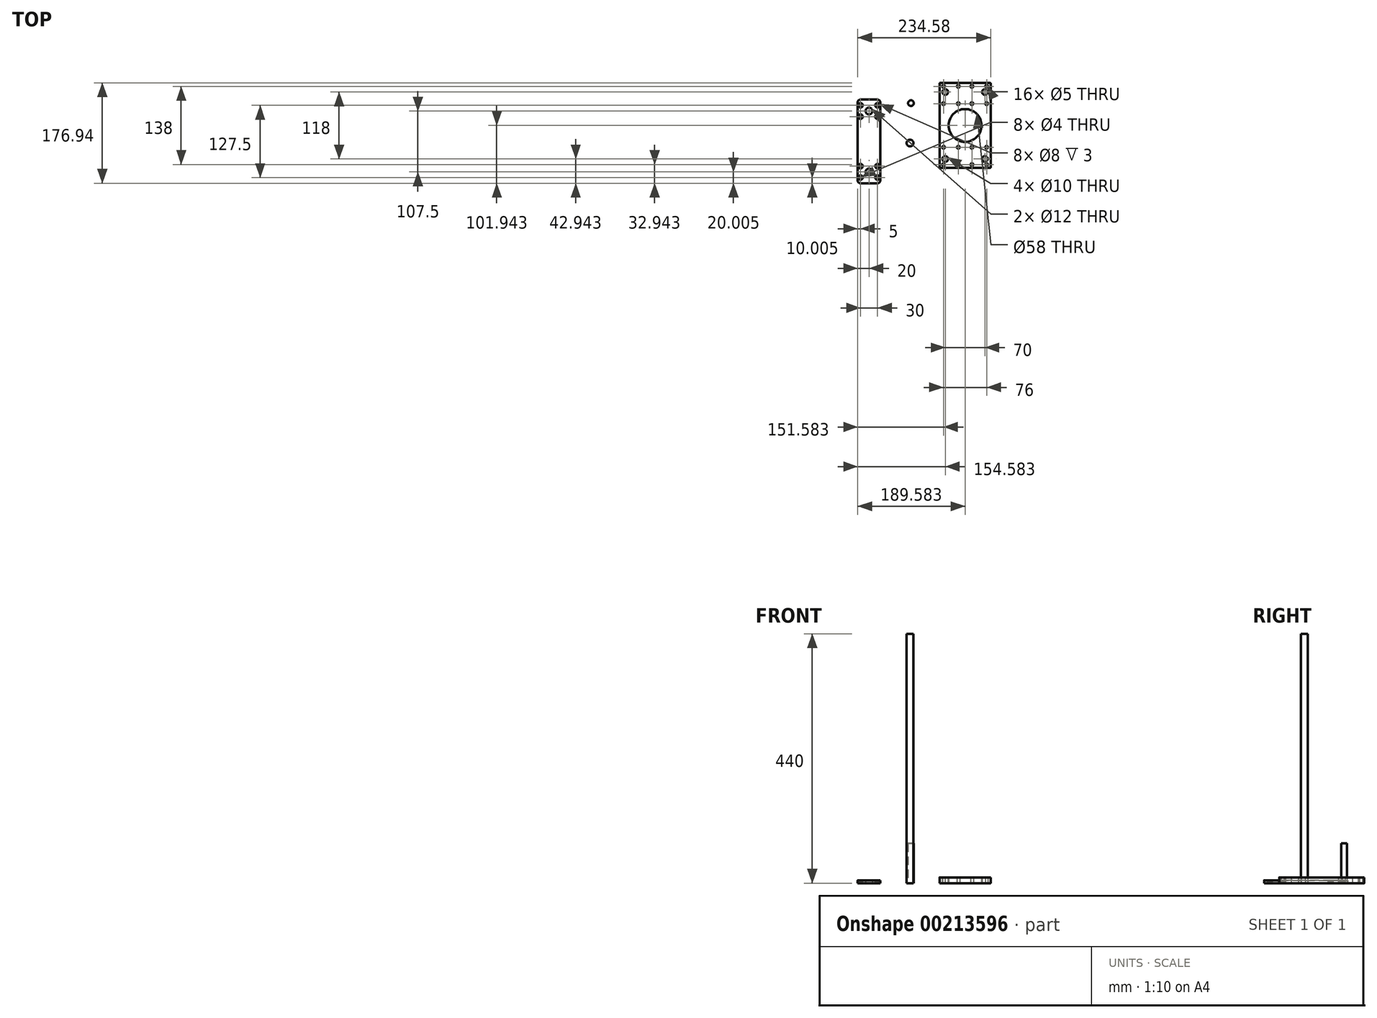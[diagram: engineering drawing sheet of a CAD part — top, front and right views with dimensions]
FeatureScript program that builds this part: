
annotation { "Feature Type Name" : "Feature", "Feature Type Description" : "" }
export const myFeature = defineFeature(function(context is Context, id is Id, definition is map)
    precondition{}
    {
        {
            var Q0;
            Q0=qCreatedBy(makeId("Top.planeOp"),FACE);
            var sketch = newSketch(context, id + "F0", { "sketchPlane" : qUnion([Q0])});
            skLineSegment(sketch, "E0", {"start": v(-47.78, -43.52) * mm, "end": v(42.22, -43.52) * mm});
            skLineSegment(sketch, "E1", {"start": v(42.22, -43.52) * mm, "end": v(42.22, 106.48) * mm});
            skLineSegment(sketch, "E2", {"start": v(42.22, 106.48) * mm, "end": v(-47.78, 106.48) * mm});
            skLineSegment(sketch, "E3", {"start": v(-47.78, 106.48) * mm, "end": v(-47.78, -43.52) * mm});
            skLineSegment(sketch, "E4", {"start": v(-2.78, 106.48) * mm, "end": v(-2.78, -43.52) * mm, "construction": true});
            skCircle(sketch, "E5", {"center": v(-2.78, 31.48) * mm, "radius": 29 * mm});
            skCircle(sketch, "E6", {"center": v(35.22, 100.48) * mm, "radius": 2.5 * mm});
            skCircle(sketch, "E7", {"center": v(35.22, 69.98) * mm, "radius": 2.5 * mm});
            skCircle(sketch, "E8", {"center": v(9.22, 100.48) * mm, "radius": 2.5 * mm});
            skCircle(sketch, "E9", {"center": v(9.22, 69.98) * mm, "radius": 2.5 * mm});
            skCircle(sketch, "E10", {"center": v(-14.78, 100.48) * mm, "radius": 2.5 * mm});
            skCircle(sketch, "E11", {"center": v(-14.78, 69.98) * mm, "radius": 2.5 * mm});
            skCircle(sketch, "E12", {"center": v(-40.78, 100.48) * mm, "radius": 2.5 * mm});
            skCircle(sketch, "E13", {"center": v(-40.78, 69.98) * mm, "radius": 2.5 * mm});
            skCircle(sketch, "E14", {"center": v(35.22, -7.02) * mm, "radius": 2.5 * mm});
            skCircle(sketch, "E15", {"center": v(35.22, -37.52) * mm, "radius": 2.5 * mm});
            skCircle(sketch, "E16", {"center": v(9.22, -7.02) * mm, "radius": 2.5 * mm});
            skCircle(sketch, "E17", {"center": v(9.22, -37.52) * mm, "radius": 2.5 * mm});
            skCircle(sketch, "E18", {"center": v(-14.78, -37.52) * mm, "radius": 2.5 * mm});
            skCircle(sketch, "E19", {"center": v(-40.78, -7.02) * mm, "radius": 2.5 * mm});
            skCircle(sketch, "E20", {"center": v(-40.78, -37.52) * mm, "radius": 2.5 * mm});
            skCircle(sketch, "E21", {"center": v(-14.78, -7.02) * mm, "radius": 2.5 * mm});
            skCircle(sketch, "E22", {"center": v(-37.78, -27.52) * mm, "radius": 5 * mm});
            skCircle(sketch, "E23", {"center": v(32.22, -27.52) * mm, "radius": 5 * mm});
            skCircle(sketch, "E24", {"center": v(32.22, 90.48) * mm, "radius": 5 * mm});
            skCircle(sketch, "E25", {"center": v(-37.78, 90.48) * mm, "radius": 5 * mm});
            skSolve(sketch);
        }
        {
            var Q0;
            Q0=makeQuery(id+"F0.imprint","IMPRINT",FACE,{"disambiguationData":[TD([[makeQuery(id+"F0.imprint","IMPRINT",EDGE,{"derivedFrom":sQuery(id+"F0.wireOp",EDGE,"E0")}),1.0]])]});
            extrude(context, id + "F1", {"entities" : qUnion([Q0]), "depth" : 10 * mm});
        }
        {
            var Q0;
            Q0=makeQuery(id+"F1.opExtrude","SWEPT_EDGE",EDGE,{"disambiguationData":[OSD([sQuery(id+"F0.wireOp",EDGE,"E0"),sQuery(id+"F0.wireOp",EDGE,"E1")])]});
            var Q1;
            Q1=makeQuery(id+"F1.opExtrude","SWEPT_EDGE",EDGE,{"disambiguationData":[OSD([sQuery(id+"F0.wireOp",EDGE,"E1"),sQuery(id+"F0.wireOp",EDGE,"E2")])]});
            var Q2;
            Q2=makeQuery(id+"F1.opExtrude","SWEPT_EDGE",EDGE,{"disambiguationData":[OSD([sQuery(id+"F0.wireOp",EDGE,"E2"),sQuery(id+"F0.wireOp",EDGE,"E3")])]});
            var Q3;
            Q3=makeQuery(id+"F1.opExtrude","SWEPT_EDGE",EDGE,{"disambiguationData":[OSD([sQuery(id+"F0.wireOp",EDGE,"E0"),sQuery(id+"F0.wireOp",EDGE,"E3")])]});
            fillet(context, id + "F2", {"entities" : qUnion([Q0, Q1, Q2, Q3]), "radius" : 1 * mm, "tangentPropagation" : true, "allowEdgeOverflow" : false});
        }
        {
            var Q0;
            Q0=qCreatedBy(makeId("Top.planeOp"),FACE);
            var sketch = newSketch(context, id + "F3", { "sketchPlane" : qUnion([Q0])});
            skCircle(sketch, "E26", {"center": v(-98.34, 70.82) * mm, "radius": 5 * mm});
            skSolve(sketch);
        }
        {
            var Q0;
            Q0=makeQuery(id+"F3.imprint","IMPRINT",FACE,{"disambiguationData":[TD([[makeQuery(id+"F3.imprint","IMPRINT",EDGE,{"derivedFrom":sQuery(id+"F3.wireOp",EDGE,"E26")}),1.0]])]});
            extrude(context, id + "F4", {"entities" : qUnion([Q0]), "depth" : 70 * mm});
        }
        {
            var Q0;
            Q0=qCreatedBy(makeId("Top.planeOp"),FACE);
            var sketch = newSketch(context, id + "F5", { "sketchPlane" : qUnion([Q0])});
            skLineSegment(sketch, "E27", {"start": v(-152.36, 77.04) * mm, "end": v(-152.36, -70.46) * mm});
            skLineSegment(sketch, "E28", {"start": v(-152.36, -70.46) * mm, "end": v(-192.36, -70.46) * mm});
            skLineSegment(sketch, "E29", {"start": v(-192.36, -70.46) * mm, "end": v(-192.36, 77.04) * mm});
            skLineSegment(sketch, "E30", {"start": v(-192.36, 77.04) * mm, "end": v(-152.36, 77.04) * mm});
            skCircle(sketch, "E31", {"center": v(-172.36, 57.04) * mm, "radius": 6 * mm});
            skCircle(sketch, "E32", {"center": v(-172.36, -50.46) * mm, "radius": 6 * mm});
            skCircle(sketch, "E33", {"center": v(-157.36, 67.04) * mm, "radius": 2 * mm});
            skCircle(sketch, "E34", {"center": v(-157.36, 47.04) * mm, "radius": 2 * mm});
            skCircle(sketch, "E35", {"center": v(-187.36, 67.04) * mm, "radius": 2 * mm});
            skCircle(sketch, "E36", {"center": v(-187.36, 47.04) * mm, "radius": 2 * mm});
            skCircle(sketch, "E37", {"center": v(-157.36, -40.46) * mm, "radius": 2 * mm});
            skCircle(sketch, "E38", {"center": v(-187.36, -40.46) * mm, "radius": 2 * mm});
            skCircle(sketch, "E39", {"center": v(-187.36, -60.46) * mm, "radius": 2 * mm});
            skCircle(sketch, "E40", {"center": v(-157.36, -60.46) * mm, "radius": 2 * mm});
            skSolve(sketch);
        }
        {
            var Q0;
            Q0=makeQuery(id+"F5.imprint","IMPRINT",FACE,{"disambiguationData":[TD([[makeQuery(id+"F5.imprint","IMPRINT",EDGE,{"derivedFrom":sQuery(id+"F5.wireOp",EDGE,"E27")}),-1.0]])]});
            extrude(context, id + "F6", {"entities" : qUnion([Q0]), "depth" : 5 * mm});
        }
        {
            var Q0;
            Q0=makeQuery(id+"F6.opExtrude","SWEPT_EDGE",EDGE,{"disambiguationData":[OSD([sQuery(id+"F5.wireOp",EDGE,"E29"),sQuery(id+"F5.wireOp",EDGE,"E30")])]});
            var Q1;
            Q1=makeQuery(id+"F6.opExtrude","SWEPT_EDGE",EDGE,{"disambiguationData":[OSD([sQuery(id+"F5.wireOp",EDGE,"E28"),sQuery(id+"F5.wireOp",EDGE,"E29")])]});
            var Q2;
            Q2=makeQuery(id+"F6.opExtrude","SWEPT_EDGE",EDGE,{"disambiguationData":[OSD([sQuery(id+"F5.wireOp",EDGE,"E27"),sQuery(id+"F5.wireOp",EDGE,"E28")])]});
            var Q3;
            Q3=makeQuery(id+"F6.opExtrude","SWEPT_EDGE",EDGE,{"disambiguationData":[OSD([sQuery(id+"F5.wireOp",EDGE,"E27"),sQuery(id+"F5.wireOp",EDGE,"E30")])]});
            fillet(context, id + "F7", {"entities" : qUnion([Q0, Q1, Q2, Q3]), "radius" : 5 * mm, "tangentPropagation" : true, "allowEdgeOverflow" : false});
        }
        {
            var Q0;
            Q0=makeQuery(id+"F6.opExtrude","CAP_FACE",FACE,{"disambiguationData":[OSD([sQuery(id+"F5.wireOp",EDGE,"E27"),sQuery(id+"F5.wireOp",EDGE,"E28"),sQuery(id+"F5.wireOp",EDGE,"E29"),sQuery(id+"F5.wireOp",EDGE,"E30"),sQuery(id+"F5.wireOp",EDGE,"E31"),sQuery(id+"F5.wireOp",EDGE,"E32"),sQuery(id+"F5.wireOp",EDGE,"E33"),sQuery(id+"F5.wireOp",EDGE,"E34"),sQuery(id+"F5.wireOp",EDGE,"E35"),sQuery(id+"F5.wireOp",EDGE,"E36"),sQuery(id+"F5.wireOp",EDGE,"E37"),sQuery(id+"F5.wireOp",EDGE,"E38"),sQuery(id+"F5.wireOp",EDGE,"E39"),sQuery(id+"F5.wireOp",EDGE,"E40")])],"isStart":false});
            var sketch = newSketch(context, id + "F8", { "sketchPlane" : qUnion([Q0])});
            skCircle(sketch, "E41", {"center": v(-157.36, 67.04) * mm, "radius": 4 * mm});
            skCircle(sketch, "E42", {"center": v(-157.36, 47.04) * mm, "radius": 4 * mm});
            skCircle(sketch, "E43", {"center": v(-187.36, 47.04) * mm, "radius": 4 * mm});
            skCircle(sketch, "E44", {"center": v(-187.36, 67.04) * mm, "radius": 4 * mm});
            skCircle(sketch, "E45", {"center": v(-187.36, -40.46) * mm, "radius": 4 * mm});
            skCircle(sketch, "E46", {"center": v(-187.36, -60.46) * mm, "radius": 4 * mm});
            skCircle(sketch, "E47", {"center": v(-157.36, -60.46) * mm, "radius": 4 * mm});
            skCircle(sketch, "E48", {"center": v(-157.36, -40.46) * mm, "radius": 4 * mm});
            skSolve(sketch);
        }
        {
            var Q0;
            Q0=makeQuery(id+"F8.imprint","IMPRINT",FACE,{"disambiguationData":[TD([[makeQuery(id+"F8.imprint","IMPRINT",EDGE,{"derivedFrom":sQuery(id+"F8.wireOp",EDGE,"E41")}),1.0]])]});
            var Q1;
            Q1=makeQuery(id+"F8.imprint","IMPRINT",FACE,{"disambiguationData":[TD([[makeQuery(id+"F8.imprint","IMPRINT",EDGE,{"derivedFrom":sQuery(id+"F8.wireOp",EDGE,"E42")}),1.0]])]});
            var Q2;
            Q2=makeQuery(id+"F8.imprint","IMPRINT",FACE,{"disambiguationData":[TD([[makeQuery(id+"F8.imprint","IMPRINT",EDGE,{"derivedFrom":sQuery(id+"F8.wireOp",EDGE,"E43")}),1.0]])]});
            var Q3;
            Q3=makeQuery(id+"F8.imprint","IMPRINT",FACE,{"disambiguationData":[TD([[makeQuery(id+"F8.imprint","IMPRINT",EDGE,{"derivedFrom":sQuery(id+"F8.wireOp",EDGE,"E44")}),1.0]])]});
            var Q4;
            Q4=makeQuery(id+"F8.imprint","IMPRINT",FACE,{"disambiguationData":[TD([[makeQuery(id+"F8.imprint","IMPRINT",EDGE,{"derivedFrom":sQuery(id+"F8.wireOp",EDGE,"E45")}),1.0]])]});
            var Q5;
            Q5=makeQuery(id+"F8.imprint","IMPRINT",FACE,{"disambiguationData":[TD([[makeQuery(id+"F8.imprint","IMPRINT",EDGE,{"derivedFrom":sQuery(id+"F8.wireOp",EDGE,"E48")}),1.0]])]});
            var Q6;
            Q6=makeQuery(id+"F8.imprint","IMPRINT",FACE,{"disambiguationData":[TD([[makeQuery(id+"F8.imprint","IMPRINT",EDGE,{"derivedFrom":sQuery(id+"F8.wireOp",EDGE,"E47")}),1.0]])]});
            var Q7;
            Q7=makeQuery(id+"F8.imprint","IMPRINT",FACE,{"disambiguationData":[TD([[makeQuery(id+"F8.imprint","IMPRINT",EDGE,{"derivedFrom":sQuery(id+"F8.wireOp",EDGE,"E46")}),1.0]])]});
            extrude(context, id + "F9", {"entities" : qUnion([Q0, Q1, Q2, Q3, Q4, Q5, Q6, Q7]), "operationType" : NewBodyOperationType.REMOVE, "oppositeDirection" : true, "depth" : 3 * mm});
        }
        {
            var Q0;
            Q0=qCreatedBy(makeId("Top.planeOp"),FACE);
            var sketch = newSketch(context, id + "F10", { "sketchPlane" : qUnion([Q0])});
            skCircle(sketch, "E49", {"center": v(-99.95, 0.49) * mm, "radius": 6 * mm});
            skSolve(sketch);
        }
        {
            var Q0;
            Q0 = qSketchRegion(id + "F10", true);
            extrude(context, id + "F11", {"entities" : qUnion([Q0]), "depth" : 440 * mm});
        }
    });
